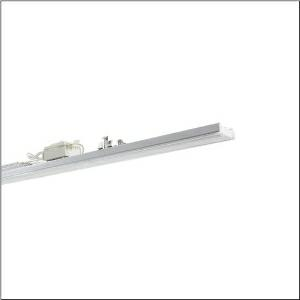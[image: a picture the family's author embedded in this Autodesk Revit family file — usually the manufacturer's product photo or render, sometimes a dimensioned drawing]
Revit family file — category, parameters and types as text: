
# Revit family: licross_r__21_recessed_mo_52te1edv4dxg_57d1
name_source: partatom
category: Lighting Fixtures
units: mm (PartAtom-declared; Revit-internal decimal feet)

## family parameters
Cut with Voids When Loaded = No
Host = Face
Light Source = No
Part Type = Normal
Room Calculation Point = No
Round Connector Dimension = Use Diameter
Shared = No

## types (1)
- --- (1 x LED, 13000 lm, 73.6 W, 4000K)
    Apparent Load = 74 VA
    CIE Flux Codes = 85 95 99 100 100
    Color Rendering = 80
    Color Temperature = 4000K
    Default Elevation = 1800 mm
    Description = Licross® 21 Recessed MO, luminaire insert, of sheet steel, galvanised, coil coated, white, length: 2.250mm, width: 66mm, height: 67mm, LED rated luminous flux: 13.000lm, light colour: 840, control gear: DALI 2, with plug, 5-pole, with phase selection, mains connection: 220..240V, AC, 50/60Hz, rated input power: 74W, halogen-free wiring, primary light control with lens, of plastic, primary optical cover: cover, of PMMA, light emission: direct distribution, primary light characteristic: symmetric, protection rating (complete): IP54, insulation class (complete): insulation class I (protective earthing), certification: CE, ENEC, VDE, UKCA, protection symbol: D if used in an environment with non-conductive dust loads with corresponding accessories, impact resistance: IK06, permissible ambient temperature for indoor applications: -25..+35°C, corresponds to IFS (International Featured Standards) requirements for safety and quality in the food industry, reducing of maximum allowable ambient temperature of 5°C with ceiling mounting, LABS conformity tested according to VDMA 24364:2018-05, packaging unit: 1 piece
    Height = 58 mm
    Lamp = 1 x LED
    Lamp Light Flux = 13000 lm
    Lamp Power = 73.6 W
    Lamp count = 1
    Length = 2250 mm
    Luminous efficacy = 177 lm/W
    Manufacturer = Siteco
    ModVariant = No
    Model = 52TE1EDV4DXG
    Mounting Place = Ceiling
    Mounting Type = Pendant
    Number of Poles = 1
    OnlyDefault = Yes
    Power Factor = 1
    Product Name = Licross® 21 Recessed MO
    Product group = luminaire insert
    ProductGroupID = 902
    Protection Class = Protection class I
    Protection Degree = IP 54
    RLX_Detail_Level = 1
    RLX_Emergency_Light_Flux = 0 lm
    RLX_Emergency_Type = 0
    RLX_Emergency_Type_DB = No
    RlxData = <blob elided: 29593 chars, md5=ffde810f>
    Socket = socket
    Standby Power = 0 W
    System Light Flux = 13000 lm
    System Power = 74 W
    Type Comments = factory setting: luminous flux: 100 % | dim-lin: 254 | 336 mA
    Type Image = l_1296930.jpg
    URL = http://relux.com
    VarID = @adj_125464
    Voltage = 0 V
    Weight = 0.00 kg
    Width = 66 mm

## geometry (parser evidence)
native form markers: Blend x4, Sweep x10
no freeform markers — native parametric forms only
